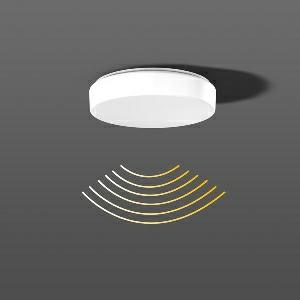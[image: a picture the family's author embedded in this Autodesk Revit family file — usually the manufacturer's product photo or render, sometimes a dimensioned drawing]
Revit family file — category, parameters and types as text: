
# Revit family: flat_polymero_kreis_311950_002_3_19_800c
name_source: partatom
category: Lighting Fixtures
units: mm (PartAtom-declared; Revit-internal decimal feet)

## family parameters
Cut with Voids When Loaded = No
Host = Face
Light Source = No
Part Type = Normal
Room Calculation Point = No
Round Connector Dimension = Use Diameter
Shared = No

## types (1)
- FLAT POLYMERO KREIS (1 x LED Modul 840, 1250 lm, 4000)
    Apparent Load = 12 VA
    CIE Flux Codes = 42 73 92 87 100
    Color Rendering = 80
    Color Temperature = 4000
    Default Elevation = 1800 mm
    Description = Series: FLAT POLYMERO KREIS
Decorative round surface-mounted luminaire. Base: metal, powder-coated. Diffuser made of non-yellowing plastic (PMMA), opal. Diffuser fastening: patented push system. Suitable for Ceiling mounting, Wall (surface). With integrated HF movement sensor. Functional parameters of a master luminaire (ceiling height of approx. 2.8 m): HF detector 24 GHz with integrated corridor function. Coverage: approx. 130° radial. Easy adjustment of functions via 3 associated push button switches. Sensitivity/Range: 0.5-5 m radial, adjustable from 10-100%. Time control 1 second to 15 minutes in 8 different levels. Daylight detection with 5 brightness levels and learning mode. Up to 9 slave luminaires can be operated with one master luminaire (max. up to 150 W / 230 W). Suitable for outdoor use to a limited extent only, as it is sensitive to all movements. 
Colour: white
Diameter: 360 mm
Height: 87 mm
Lamp: LED exchangeable
Socket: without socket
Colour temperature: 4000K
Colour rendering index (CRI): 83
System power: 12 W
Rated luminous flux: 1250 lm
Luminous efficiency: 104 lm/W
Control gear: Converter not necessary
Protection class: I
Type of protection: IP 40
    Height = 87 mm
    Lamp = 1 x LED Modul 840
    Lamp Light Flux = 1250 lm
    Lamp count = 1
    Length = 360 mm
    Lifetime = 50000 h
    Luminous efficacy = 104 lm/W
    Manufacturer = RZB
    ModVariant = No
    Model = 311950.002.3.19
    Mounting Place = Ceiling, Wall
    Mounting Type = Surface mounted
    Number of Poles = 1
    OnlyDefault = Yes
    Power Factor = 1
    Product Name = FLAT POLYMERO KREIS
    Product group = Surface mounted ceiling and wall luminaires
    ProductGroupID = 305
    Protection Class = Protection class I
    Protection Degree = IP 40
    RLX_Detail_Level = 1
    RLX_Emergency_Light_Flux = 0 lm
    RLX_Emergency_Type = 0
    RLX_Emergency_Type_DB = No
    RlxData = <blob elided: 67361 chars, md5=d4f92d6d>
    Socket = socket
    Standby Power = 0 W
    System Light Flux = 1250 lm
    System Power = 12 W
    Type Comments = Product without accessories
    Type Image = 311599.002.19.jpg
    URL = http://relux.com
    VarID = ---
    Voltage = 230 V
    Voltage Range = 220-240 V
    Weight = 0.00 kg
    Width = 0 mm  [stored 0 ft]

note: [stored X ft] marks values corroborated as IEEE doubles in the binary element streams (Revit-internal decimal feet)

## geometry (parser evidence)
native form markers: Blend x4, Sweep x13
no freeform markers — native parametric forms only
